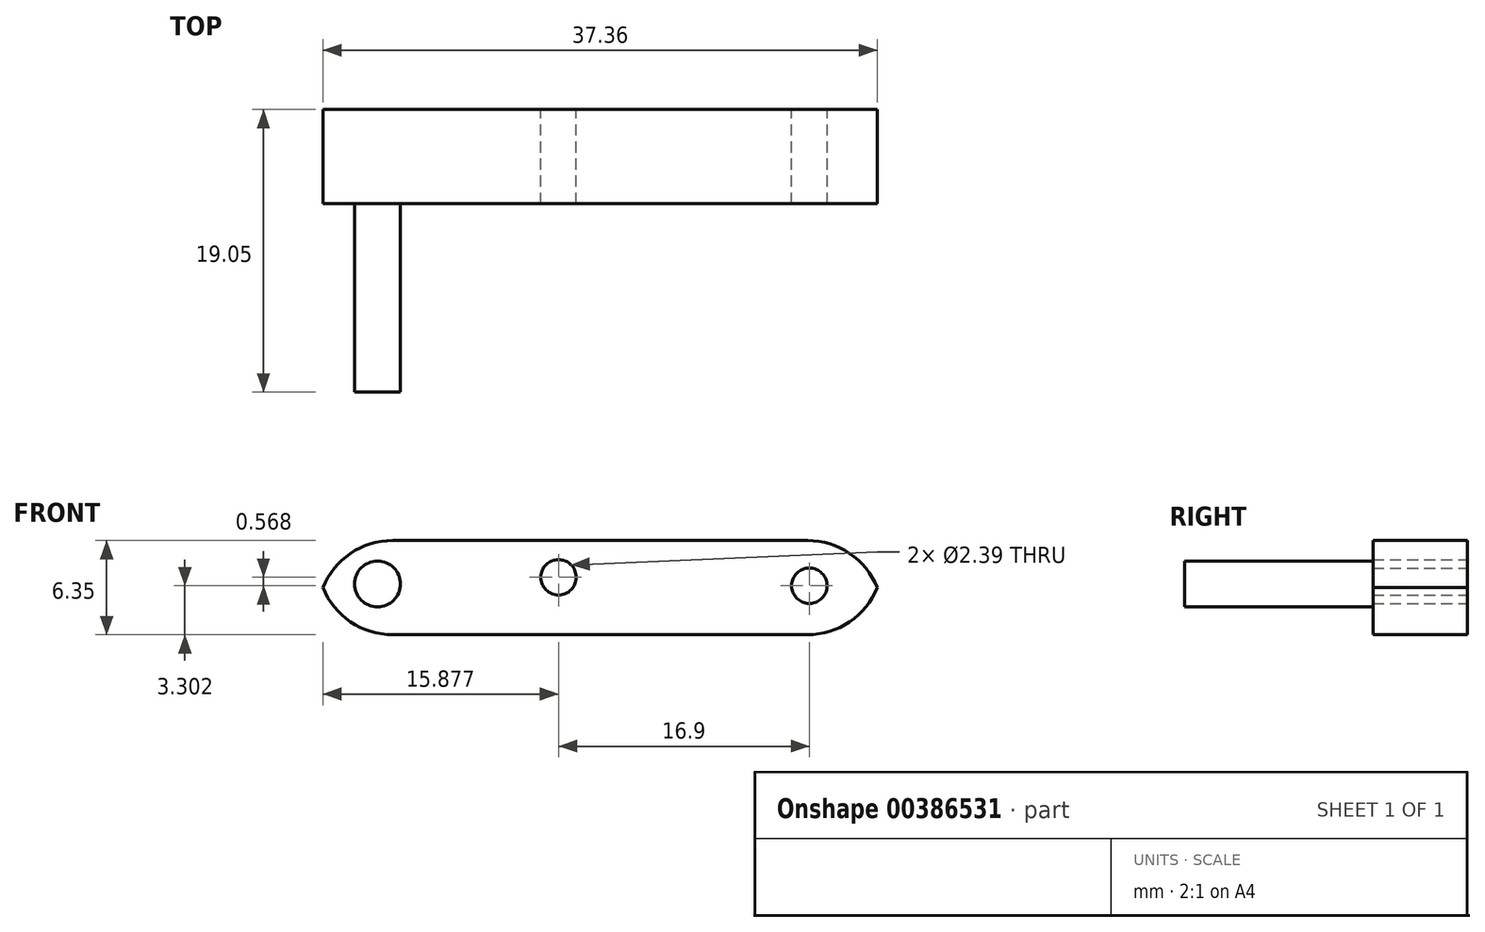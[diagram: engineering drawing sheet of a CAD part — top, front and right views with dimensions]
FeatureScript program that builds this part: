
annotation { "Feature Type Name" : "Feature", "Feature Type Description" : "" }
export const myFeature = defineFeature(function(context is Context, id is Id, definition is map)
    precondition{}
    {
        {
            var Q0;
            Q0=qCreatedBy(makeId("Front.planeOp"),FACE);
            var sketch = newSketch(context, id + "F0", { "sketchPlane" : qUnion([Q0])});
            skLineSegment(sketch, "E0.bottom", {"start": v(0, 0) * mm, "end": v(38.1, 0) * mm});
            skLineSegment(sketch, "E0.top", {"start": v(0, 6.35) * mm, "end": v(38.1, 6.35) * mm});
            skLineSegment(sketch, "E0.left", {"start": v(0, 0) * mm, "end": v(0, 6.35) * mm});
            skLineSegment(sketch, "E0.right", {"start": v(38.1, 0) * mm, "end": v(38.1, 6.35) * mm});
            skCircle(sketch, "E1", {"center": v(3.18, 3.18) * mm, "radius": 2.54 * mm, "construction": true});
            skPoint(sketch, "E1.centerSnap0", {"position": v(38.1, 3.18) * mm});
            skCircle(sketch, "E2", {"center": v(16.25, 3.87) * mm, "radius": 1.2 * mm});
            skCircle(sketch, "E3", {"center": v(33.15, 3.3) * mm, "radius": 1.2 * mm});
            skSolve(sketch);
        }
        {
            var Q0;
            Q0 = qSketchRegion(id + "F0", true);
            extrude(context, id + "F1", {"entities" : qUnion([Q0]), "depth" : 6.35 * mm});
        }
        {
            var Q0;
            Q0=makeQuery(id+"F1.opExtrude","SWEPT_EDGE",EDGE,{"disambiguationData":[OSD([sQuery(id+"F0.wireOp",EDGE,"E0.top"),sQuery(id+"F0.wireOp",EDGE,"E0.left")])]});
            var Q1;
            Q1=makeQuery(id+"F1.opExtrude","SWEPT_EDGE",EDGE,{"disambiguationData":[OSD([sQuery(id+"F0.wireOp",EDGE,"E0.bottom"),sQuery(id+"F0.wireOp",EDGE,"E0.left")])]});
            var Q2;
            Q2=makeQuery(id+"F1.opExtrude","SWEPT_EDGE",EDGE,{"disambiguationData":[OSD([sQuery(id+"F0.wireOp",EDGE,"E0.top"),sQuery(id+"F0.wireOp",EDGE,"E0.right")])]});
            var Q3;
            Q3=makeQuery(id+"F1.opExtrude","SWEPT_EDGE",EDGE,{"disambiguationData":[OSD([sQuery(id+"F0.wireOp",EDGE,"E0.bottom"),sQuery(id+"F0.wireOp",EDGE,"E0.right")])]});
            fillet(context, id + "F2", {"entities" : qUnion([Q0, Q1, Q2, Q3]), "radius" : 5.08 * mm, "tangentPropagation" : true, "allowEdgeOverflow" : false});
        }
        {
            var Q0;
            Q0=makeQuery(id+"F1.opExtrude","CAP_FACE",FACE,{"disambiguationData":[OSD([sQuery(id+"F0.wireOp",EDGE,"E0.bottom"),sQuery(id+"F0.wireOp",EDGE,"E0.top"),sQuery(id+"F0.wireOp",EDGE,"E0.left"),sQuery(id+"F0.wireOp",EDGE,"E0.right"),sQuery(id+"F0.wireOp",EDGE,"E2"),sQuery(id+"F0.wireOp",EDGE,"E3")])],"isStart":false});
            var sketch = newSketch(context, id + "F3", { "sketchPlane" : qUnion([Q0])});
            skCircle(sketch, "E4", {"center": v(4.06, 3.42) * mm, "radius": 1.55 * mm});
            skSolve(sketch);
        }
        {
            var Q0;
            Q0 = qSketchRegion(id + "F3", true);
            extrude(context, id + "F4", {"entities" : qUnion([Q0]), "operationType" : NewBodyOperationType.ADD, "depth" : 12.7 * mm});
        }
    });
